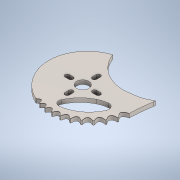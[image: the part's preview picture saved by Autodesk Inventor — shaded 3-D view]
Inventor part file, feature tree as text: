
AUTODESK INVENTOR PART (.ipt)
format: ipt  version: 2020 (Build 240168000, 168)  size: 306,688 bytes
history: native  units: in
note: dims shown in document units (in); Inventor stores cm internally (conversion verified against a paired STEP export)
features: extrude x1, sketch x1, projected_geometry x1, other x1
ambient origin geometry x8: Origin, YZ Plane, XZ Plane, XY Plane, X Axis, Y Axis, Z Axis, Center Point
bodies: Solid1 (feature_tree)
feature tree (4):
  extrude  "Extrusion1"  [1 undecoded]
  sketch  "Sketch1"  dims[d0=0.0118in d1=0.0in]
  projected_geometry  "Projected Loop1"
  other  "Body-Move_Copy2"
note: 1 required parameter value undecoded (feature->parameter linkage not recoverable at this tier; creation-order binding heuristic only, values carry confidence <= 0.55)
